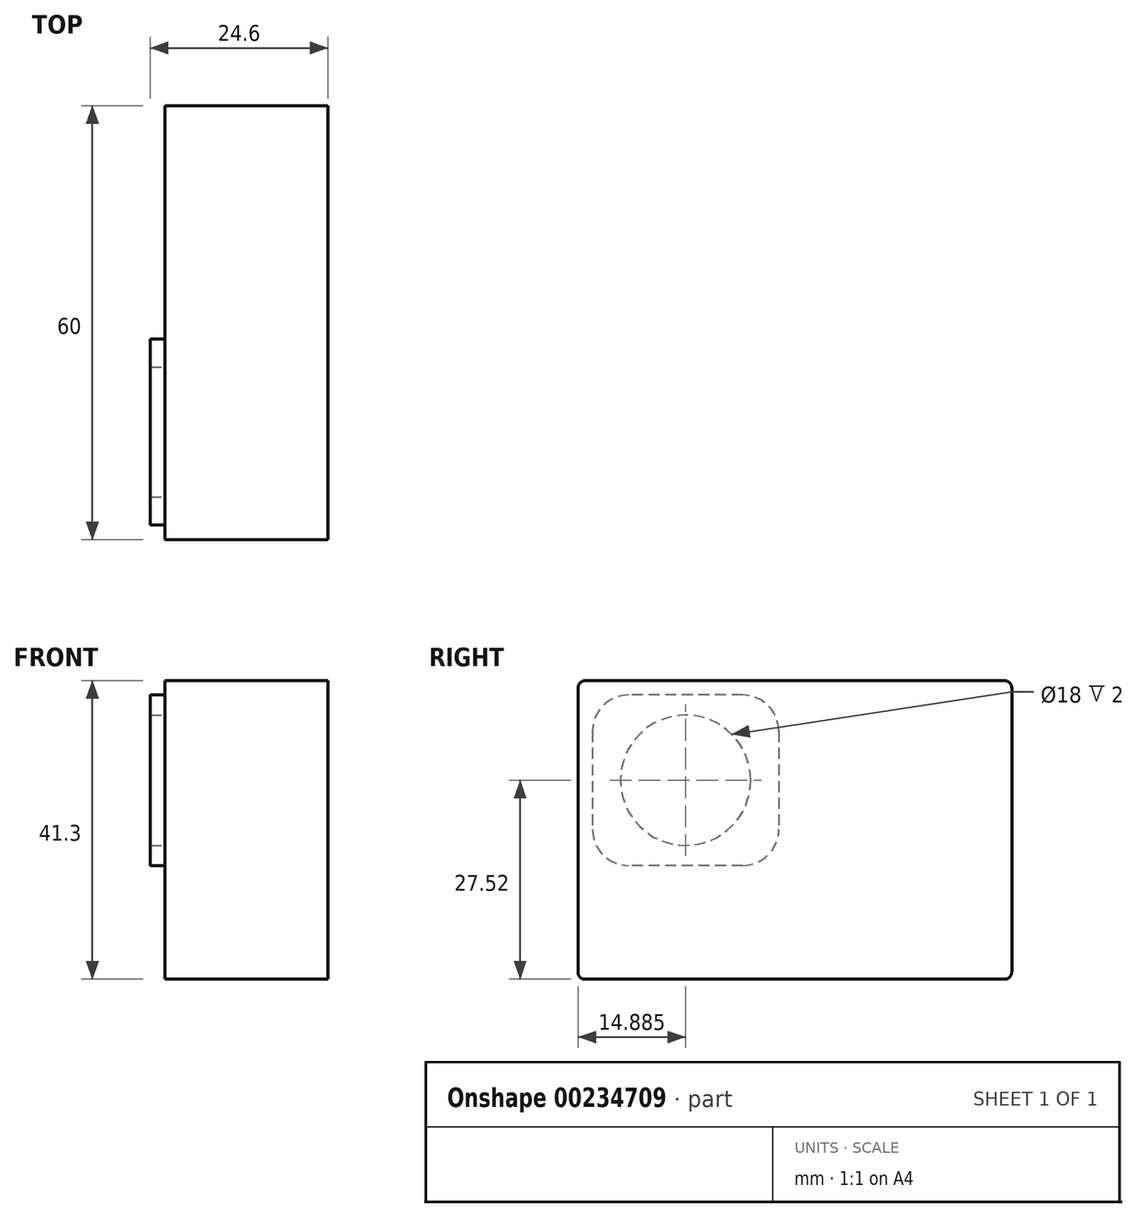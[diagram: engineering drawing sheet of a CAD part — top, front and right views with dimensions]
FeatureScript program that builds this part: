
annotation { "Feature Type Name" : "Feature", "Feature Type Description" : "" }
export const myFeature = defineFeature(function(context is Context, id is Id, definition is map)
    precondition{}
    {
        {
            var Q0;
            Q0=qCreatedBy(makeId("Right.planeOp"),FACE);
            var sketch = newSketch(context, id + "F0", { "sketchPlane" : qUnion([Q0])});
            skLineSegment(sketch, "E0.bottom", {"start": v(0, 0) * mm, "end": v(60, 0) * mm});
            skLineSegment(sketch, "E0.top", {"start": v(0, 41.3) * mm, "end": v(60, 41.3) * mm});
            skLineSegment(sketch, "E0.left", {"start": v(0, 0) * mm, "end": v(0, 41.3) * mm});
            skLineSegment(sketch, "E0.right", {"start": v(60, 0) * mm, "end": v(60, 41.3) * mm});
            skSolve(sketch);
        }
        {
            var Q0;
            Q0=makeQuery(id+"F0.imprint","IMPRINT",FACE,{"disambiguationData":[TD([[makeQuery(id+"F0.imprint","IMPRINT",EDGE,{"derivedFrom":sQuery(id+"F0.wireOp",EDGE,"E0.bottom")}),1.0]])]});
            extrude(context, id + "F1", {"entities" : qUnion([Q0]), "depth" : 22.6 * mm});
        }
        {
            var Q0;
            Q0=makeQuery(id+"F1.opExtrude","SWEPT_EDGE",EDGE,{"disambiguationData":[OSD([sQuery(id+"F0.wireOp",EDGE,"E0.top"),sQuery(id+"F0.wireOp",EDGE,"E0.right")])]});
            var Q1;
            Q1=makeQuery(id+"F1.opExtrude","SWEPT_EDGE",EDGE,{"disambiguationData":[OSD([sQuery(id+"F0.wireOp",EDGE,"E0.top"),sQuery(id+"F0.wireOp",EDGE,"E0.left")])]});
            var Q2;
            Q2=makeQuery(id+"F1.opExtrude","SWEPT_EDGE",EDGE,{"disambiguationData":[OSD([sQuery(id+"F0.wireOp",EDGE,"E0.bottom"),sQuery(id+"F0.wireOp",EDGE,"E0.left")])]});
            var Q3;
            Q3=makeQuery(id+"F1.opExtrude","SWEPT_EDGE",EDGE,{"disambiguationData":[OSD([sQuery(id+"F0.wireOp",EDGE,"E0.bottom"),sQuery(id+"F0.wireOp",EDGE,"E0.right")])]});
            fillet(context, id + "F2", {"entities" : qUnion([Q0, Q1, Q2, Q3]), "radius" : 1 * mm, "tangentPropagation" : true, "allowEdgeOverflow" : false});
        }
        {
            var Q0;
            Q0=makeQuery(id+"F1.opExtrude","CAP_FACE",FACE,{"disambiguationData":[OSD([sQuery(id+"F0.wireOp",EDGE,"E0.bottom"),sQuery(id+"F0.wireOp",EDGE,"E0.top"),sQuery(id+"F0.wireOp",EDGE,"E0.left"),sQuery(id+"F0.wireOp",EDGE,"E0.right")])],"isStart":true});
            var sketch = newSketch(context, id + "F3", { "sketchPlane" : qUnion([Q0])});
            skLineSegment(sketch, "E1.bottom", {"start": v(-27.77, 39.3) * mm, "end": v(-2, 39.3) * mm});
            skLineSegment(sketch, "E1.top", {"start": v(-27.77, 15.74) * mm, "end": v(-2, 15.74) * mm});
            skLineSegment(sketch, "E1.left", {"start": v(-27.77, 39.3) * mm, "end": v(-27.77, 15.74) * mm});
            skLineSegment(sketch, "E1.right", {"start": v(-2, 39.3) * mm, "end": v(-2, 15.74) * mm});
            skCircle(sketch, "E2", {"center": v(-14.88, 27.52) * mm, "radius": 9 * mm});
            skSolve(sketch);
        }
        {
            var Q0;
            Q0=makeQuery(id+"F3.imprint","IMPRINT",FACE,{"disambiguationData":[TD([[makeQuery(id+"F3.imprint","IMPRINT",EDGE,{"derivedFrom":sQuery(id+"F3.wireOp",EDGE,"E1.bottom")}),-1.0]])]});
            extrude(context, id + "F4", {"entities" : qUnion([Q0]), "operationType" : NewBodyOperationType.ADD, "depth" : 2 * mm});
        }
        {
            var Q0;
            Q0=makeQuery(id+"F4.opExtrude","SWEPT_EDGE",EDGE,{"disambiguationData":[OSD([sQuery(id+"F3.wireOp",EDGE,"E1.bottom"),sQuery(id+"F3.wireOp",EDGE,"E1.right")])]});
            var Q1;
            Q1=makeQuery(id+"F4.opExtrude","SWEPT_EDGE",EDGE,{"disambiguationData":[OSD([sQuery(id+"F3.wireOp",EDGE,"E1.top"),sQuery(id+"F3.wireOp",EDGE,"E1.right")])]});
            var Q2;
            Q2=makeQuery(id+"F4.opExtrude","SWEPT_EDGE",EDGE,{"disambiguationData":[OSD([sQuery(id+"F3.wireOp",EDGE,"E1.top"),sQuery(id+"F3.wireOp",EDGE,"E1.left")])]});
            var Q3;
            Q3=makeQuery(id+"F4.opExtrude","SWEPT_EDGE",EDGE,{"disambiguationData":[OSD([sQuery(id+"F3.wireOp",EDGE,"E1.bottom"),sQuery(id+"F3.wireOp",EDGE,"E1.left")])]});
            fillet(context, id + "F5", {"entities" : qUnion([Q0, Q1, Q2, Q3]), "radius" : 5 * mm, "tangentPropagation" : true, "allowEdgeOverflow" : false});
        }
    });
